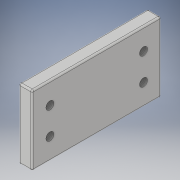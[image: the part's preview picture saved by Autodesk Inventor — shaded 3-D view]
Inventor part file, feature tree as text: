
AUTODESK INVENTOR PART (.ipt)
format: ipt  version: 2019 (Build 230136000, 136)  size: 129,536 bytes
history: native  units: in
note: dims shown in document units (in); Inventor stores cm internally (conversion verified against a paired STEP export)
features: extrude x2, mirror x2, thread x1, fillet x1, sketch x1
ambient origin geometry x8: Origin, YZ Plane, XZ Plane, XY Plane, X Axis, Y Axis, Z Axis, Center Point
bodies: Solid1 (feature_tree)
feature tree (7):
  extrude  "Extrusion1"  Depth=1.0236in
  extrude  "Extrusion2"  Depth=0.1969in TaperAngle=0.0deg
  thread  "Thread1"  [1 undecoded]
  mirror  "Mirror1"
  fillet  "Fillet1"  Radius=0.1969in
  mirror  "Mirror2"
  sketch  "Sketch1"  dims[d0=1.8898in d1=1.0236in d2=0.1969in d3=0.0in d5=0.1181in d6=0.1969in d7=0.0in d8=0.3937in d9=0.0in d10=0.0236in d11=0.6853in d12=0.1969in]
note: 1 required parameter value undecoded (feature->parameter linkage not recoverable at this tier; creation-order binding heuristic only, values carry confidence <= 0.55)
